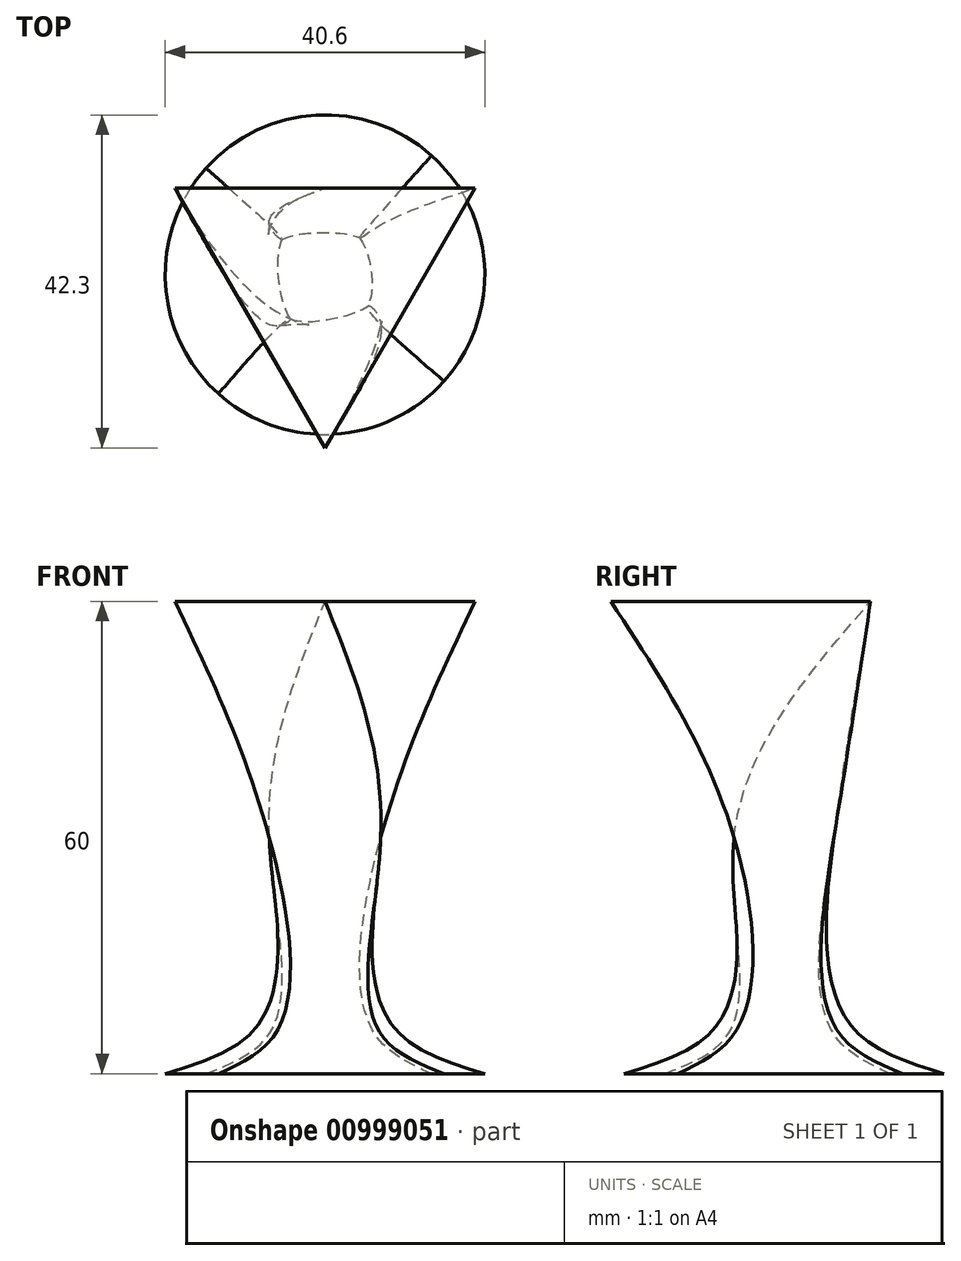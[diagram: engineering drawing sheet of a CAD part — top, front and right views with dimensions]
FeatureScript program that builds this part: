
annotation { "Feature Type Name" : "Feature", "Feature Type Description" : "" }
export const myFeature = defineFeature(function(context is Context, id is Id, definition is map)
    precondition{}
    {
        {
            var Q0;
            Q0=qCreatedBy(makeId("Top.planeOp"),FACE);
            var sketch = newSketch(context, id + "F0", { "sketchPlane" : qUnion([Q0])});
            skCircle(sketch, "E0", {"center": v(0, 0) * mm, "radius": 20.3 * mm});
            skSolve(sketch);
        }
        {
            var Q0;
            Q0=qCreatedBy(makeId("Top.planeOp"),FACE);
            cPlane(context, id + "F1", {"entities" : qUnion([Q0]), "cplaneType" : CPlaneType.OFFSET, "offset" : 30 * mm, "width" : 152.4 * mm, "height" : 152.4 * mm});
        }
        {
            var Q0;
            Q0=qCreatedBy(id+"F1.planeOp",FACE);
            var sketch = newSketch(context, id + "F2", { "sketchPlane" : qUnion([Q0])});
            skLineSegment(sketch, "E1.bottom", {"start": v(7.08, -6.34) * mm, "end": v(-7.08, -6.34) * mm});
            skLineSegment(sketch, "E1.top", {"start": v(7.08, 6.34) * mm, "end": v(-7.08, 6.34) * mm});
            skLineSegment(sketch, "E1.left", {"start": v(7.08, -6.34) * mm, "end": v(7.08, 6.34) * mm});
            skLineSegment(sketch, "E1.right", {"start": v(-7.08, -6.34) * mm, "end": v(-7.08, 6.34) * mm});
            skPoint(sketch, "E1.middle", {"position": v(0, 0) * mm});
            skSolve(sketch);
        }
        {
            var Q0;
            Q0=qCreatedBy(id+"F1.planeOp",FACE);
            cPlane(context, id + "F3", {"entities" : qUnion([Q0]), "cplaneType" : CPlaneType.OFFSET, "offset" : 30 * mm, "width" : 152.4 * mm, "height" : 152.4 * mm});
        }
        {
            var Q0;
            Q0=qCreatedBy(id+"F3.planeOp",FACE);
            var sketch = newSketch(context, id + "F4", { "sketchPlane" : qUnion([Q0])});
            skCircle(sketch, "E2.cCircle", {"center": v(0, 0) * mm, "radius": 11 * mm, "construction": true});
            skLineSegment(sketch, "E2.0", {"start": v(-19.05, 11) * mm, "end": v(19.05, 11) * mm});
            skLineSegment(sketch, "E2.1", {"start": v(19.05, 11) * mm, "end": v(0, -22) * mm});
            skLineSegment(sketch, "E2.2", {"start": v(0, -22) * mm, "end": v(-19.05, 11) * mm});
            skPoint(sketch, "E2.0.midPoint", {"position": v(0, 11) * mm});
            skSolve(sketch);
        }
        {
            var Q0;
            Q0=qCreatedBy(makeId("Top.planeOp"),FACE);
            cPlane(context, id + "F5", {"entities" : qUnion([Q0]), "cplaneType" : CPlaneType.OFFSET, "offset" : 5 * mm, "width" : 152.4 * mm, "height" : 152.4 * mm});
        }
        {
            var Q0;
            Q0=qCreatedBy(id+"F5.planeOp",FACE);
            var sketch = newSketch(context, id + "F6", { "sketchPlane" : qUnion([Q0])});
            skCircle(sketch, "E3", {"center": v(0, 0) * mm, "radius": 9.53 * mm});
            skSolve(sketch);
        }
        {
            var Q0;
            Q0=makeQuery(id+"F0.imprint","IMPRINT",FACE,{"disambiguationData":[TD([[makeQuery(id+"F0.imprint","IMPRINT",EDGE,{"derivedFrom":sQuery(id+"F0.wireOp",EDGE,"E0")}),1.0]])]});
            var Q1;
            Q1=makeQuery(id+"F6.imprint","IMPRINT",FACE,{"disambiguationData":[TD([[makeQuery(id+"F6.imprint","IMPRINT",EDGE,{"derivedFrom":sQuery(id+"F6.wireOp",EDGE,"E3")}),1.0]])]});
            var Q2;
            Q2=makeQuery(id+"F2.imprint","IMPRINT",FACE,{"disambiguationData":[TD([[makeQuery(id+"F2.imprint","IMPRINT",EDGE,{"derivedFrom":sQuery(id+"F2.wireOp",EDGE,"E1.bottom")}),-1.0]])]});
            var Q3;
            Q3=makeQuery(id+"F4.imprint","IMPRINT",FACE,{"disambiguationData":[TD([[makeQuery(id+"F4.imprint","IMPRINT",EDGE,{"derivedFrom":sQuery(id+"F4.wireOp",EDGE,"E2.0")}),-1.0]])]});
            loft(context, id + "F7", {"sheetProfilesArray" : [{ "sheetProfileEntities" : qUnion([Q0]) }, { "sheetProfileEntities" : qUnion([Q1]) }, { "sheetProfileEntities" : qUnion([Q2]) }, { "sheetProfileEntities" : qUnion([Q3]) }]});
        }
    });
